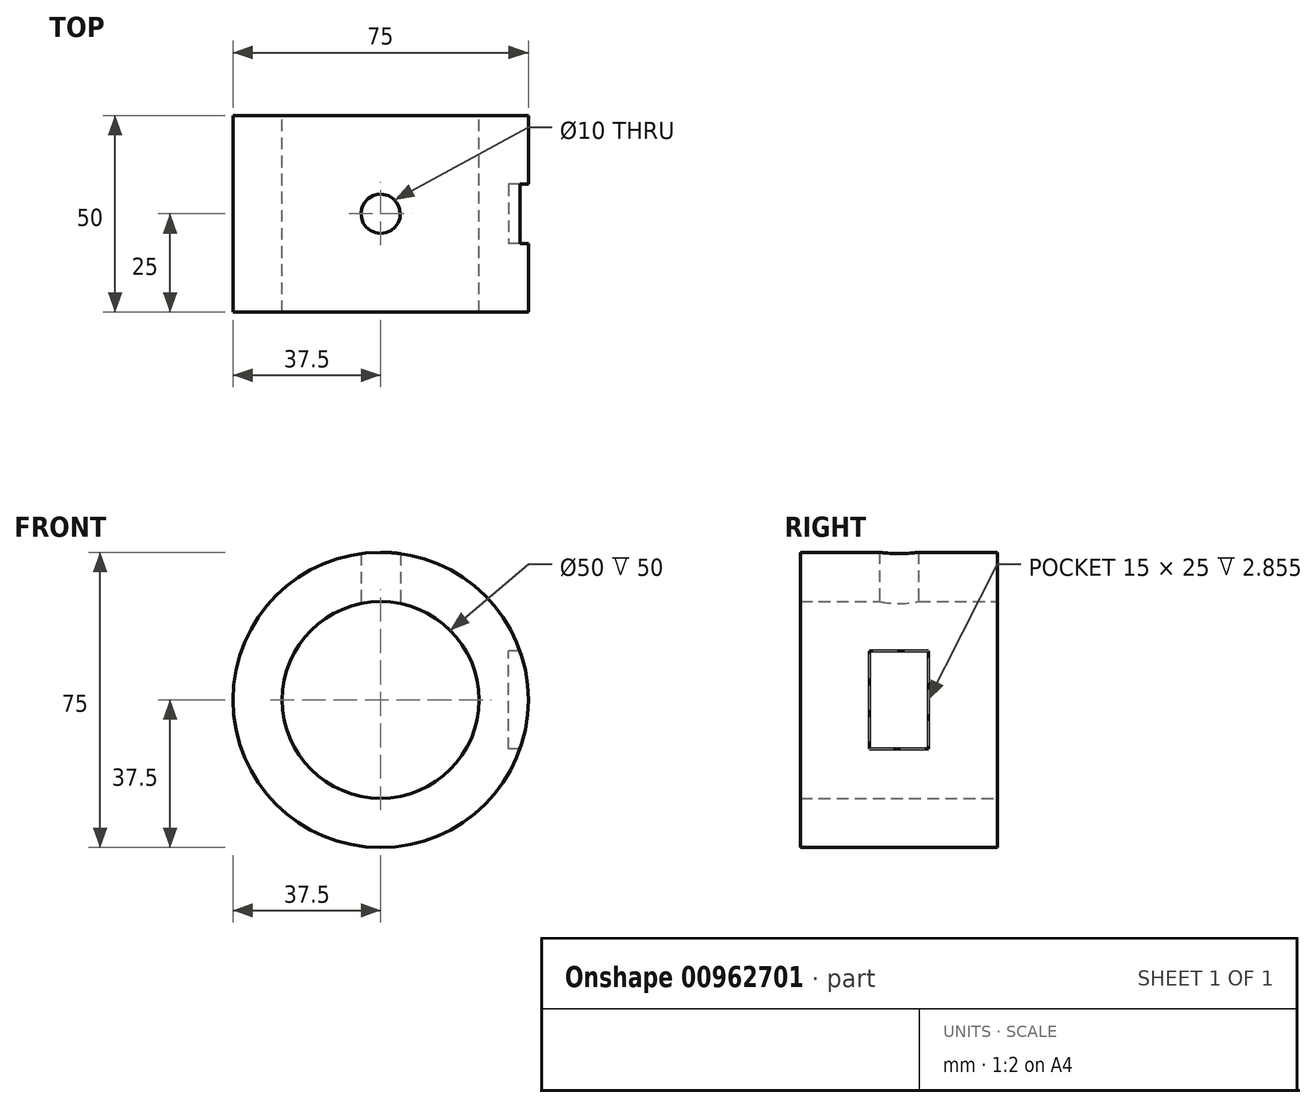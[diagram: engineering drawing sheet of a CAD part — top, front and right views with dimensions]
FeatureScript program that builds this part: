
annotation { "Feature Type Name" : "Feature", "Feature Type Description" : "" }
export const myFeature = defineFeature(function(context is Context, id is Id, definition is map)
    precondition{}
    {
        {
            var Q0;
            Q0=qCreatedBy(makeId("Front.planeOp"),FACE);
            var sketch = newSketch(context, id + "F0", { "sketchPlane" : qUnion([Q0])});
            skCircle(sketch, "E0", {"center": v(0, 0) * mm, "radius": 25 * mm});
            skCircle(sketch, "E1", {"center": v(0, 0) * mm, "radius": 37.5 * mm});
            skSolve(sketch);
        }
        {
            var Q0;
            Q0=makeQuery(id+"F0.imprint","IMPRINT",FACE,{"disambiguationData":[TD([[makeQuery(id+"F0.imprint","IMPRINT",EDGE,{"derivedFrom":sQuery(id+"F0.wireOp",EDGE,"E0")}),-1.0]])]});
            extrude(context, id + "F1", {"entities" : qUnion([Q0]), "endBound" : BoundingType.SYMMETRIC, "depth" : 50 * mm, "offsetDistance" : 25 * mm});
        }
        {
            var Q0;
            Q0=qCreatedBy(makeId("Top.planeOp"),FACE);
            var sketch = newSketch(context, id + "F2", { "sketchPlane" : qUnion([Q0])});
            skCircle(sketch, "E2", {"center": v(0, 0) * mm, "radius": 5 * mm});
            skLineSegment(sketch, "E3", {"start": v(37.5, 25) * mm, "end": v(37.5, -25) * mm});
            skLineSegment(sketch, "E4.bottom", {"start": v(42.5, 7.5) * mm, "end": v(32.5, 7.5) * mm});
            skLineSegment(sketch, "E4.top", {"start": v(42.5, -7.5) * mm, "end": v(32.5, -7.5) * mm});
            skLineSegment(sketch, "E4.left", {"start": v(42.5, 7.5) * mm, "end": v(42.5, -7.5) * mm});
            skLineSegment(sketch, "E4.right", {"start": v(32.5, 7.5) * mm, "end": v(32.5, -7.5) * mm});
            skPoint(sketch, "E4.middle", {"position": v(37.5, 0) * mm});
            skLineSegment(sketch, "E5", {"start": v(0, 28.6) * mm, "end": v(0, -28.42) * mm, "construction": true});
            skLineSegment(sketch, "E6.MirrorCS", {"start": v(-42.5, -7.5) * mm, "end": v(-32.5, -7.5) * mm});
            skLineSegment(sketch, "E7.MirrorCS", {"start": v(-42.5, 7.5) * mm, "end": v(-42.5, -7.5) * mm});
            skLineSegment(sketch, "E8.MirrorCS", {"start": v(-42.5, 7.5) * mm, "end": v(-32.5, 7.5) * mm});
            skPoint(sketch, "E9.MirrorP", {"position": v(-37.5, 0) * mm});
            skLineSegment(sketch, "E10.MirrorCS", {"start": v(-32.5, 7.5) * mm, "end": v(-32.5, -7.5) * mm});
            skLineSegment(sketch, "E11.0", {"start": v(37.5, -25) * mm, "end": v(-37.5, -25) * mm});
            skLineSegment(sketch, "E12.bottom", {"start": v(37.5, -35) * mm, "end": v(-37.5, -35) * mm});
            skLineSegment(sketch, "E12.top", {"start": v(37.5, -15) * mm, "end": v(-37.5, -15) * mm});
            skLineSegment(sketch, "E12.left", {"start": v(37.5, -35) * mm, "end": v(37.5, -15) * mm});
            skLineSegment(sketch, "E12.right", {"start": v(-37.5, -35) * mm, "end": v(-37.5, -15) * mm});
            skPoint(sketch, "E12.middle", {"position": v(0, -25) * mm});
            skLineSegment(sketch, "E13", {"start": v(-53.25, 0) * mm, "end": v(63.69, 0) * mm, "construction": true});
            skPoint(sketch, "E13.endSnap0", {"position": v(42.5, 0) * mm});
            skSolve(sketch);
        }
        {
            var Q0;
            Q0=makeQuery(id+"F2.imprint","IMPRINT",FACE,{"disambiguationData":[TD([[makeQuery(id+"F2.imprint","IMPRINT",EDGE,{"derivedFrom":sQuery(id+"F2.wireOp",EDGE,"E2")}),1.0]])]});
            extrude(context, id + "F3", {"entities" : qUnion([Q0]), "operationType" : NewBodyOperationType.REMOVE, "endBound" : BoundingType.THROUGH_ALL, "depth" : 25 * mm, "offsetDistance" : 25 * mm});
        }
        {
            var Q0;
            {var subQ5=sQuery(id+"F2.wireOp",EDGE,"E4.right");Q0=makeQuery(id+"F2.imprint","IMPRINT",FACE,{"disambiguationData":[TD([[makeQuery(id+"F2.imprint","IMPRINT",EDGE,{"derivedFrom":subQ5}),1.0]])]});}
            extrude(context, id + "F4", {"entities" : qUnion([Q0]), "operationType" : NewBodyOperationType.REMOVE, "endBound" : BoundingType.SYMMETRIC, "oppositeDirection" : true, "depth" : 25 * mm, "offsetDistance" : 25 * mm});
        }
    });
